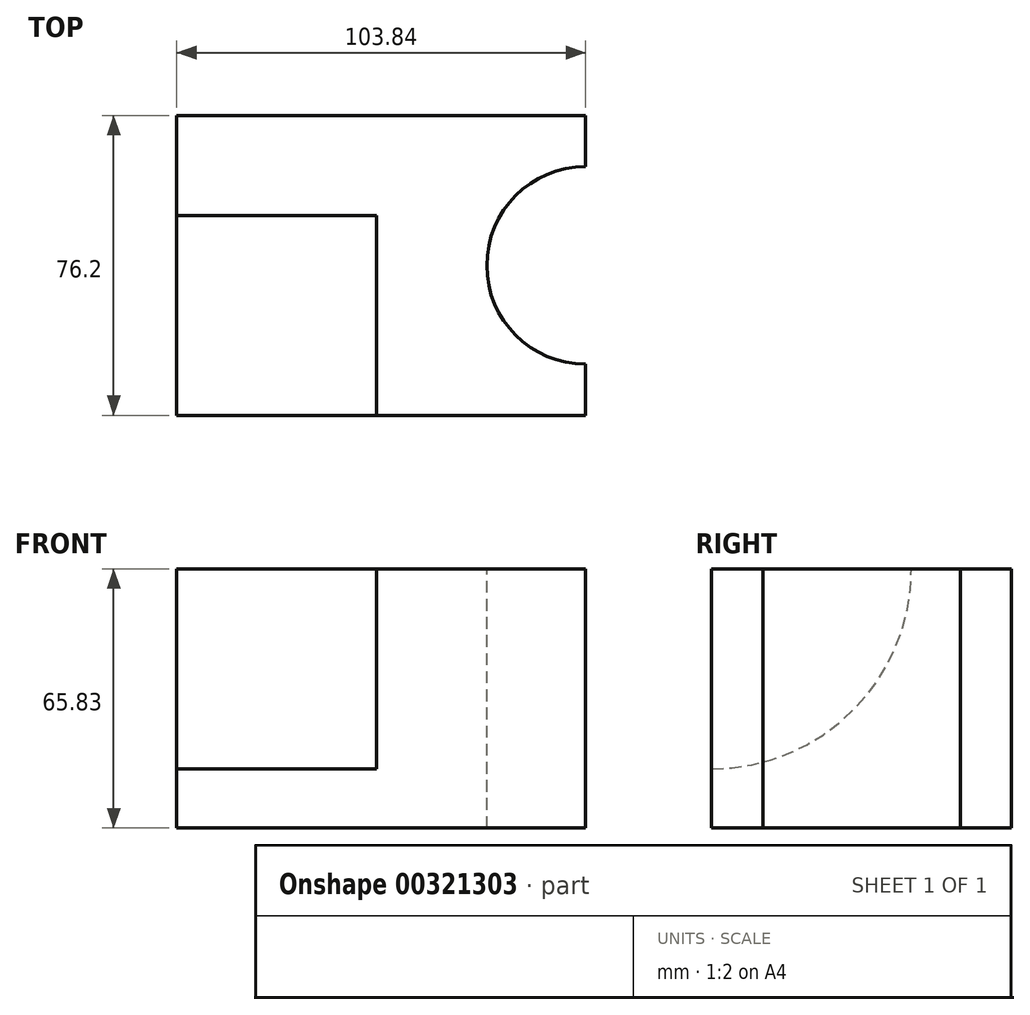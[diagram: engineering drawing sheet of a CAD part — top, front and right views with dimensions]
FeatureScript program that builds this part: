
annotation { "Feature Type Name" : "Feature", "Feature Type Description" : "" }
export const myFeature = defineFeature(function(context is Context, id is Id, definition is map)
    precondition{}
    {
        {
            var Q0;
            Q0=qCreatedBy(makeId("Front.planeOp"),FACE);
            var sketch = newSketch(context, id + "F0", { "sketchPlane" : qUnion([Q0])});
            skLineSegment(sketch, "E0", {"start": v(-57.31, -31.78) * mm, "end": v(46.53, -31.78) * mm});
            skLineSegment(sketch, "E1", {"start": v(46.53, -31.78) * mm, "end": v(46.53, 34.05) * mm});
            skLineSegment(sketch, "E2", {"start": v(46.53, 34.05) * mm, "end": v(-57.31, 34.05) * mm});
            skLineSegment(sketch, "E3", {"start": v(-57.31, 34.05) * mm, "end": v(-57.31, -31.78) * mm});
            skSolve(sketch);
        }
        {
            var Q0;
            Q0 = qSketchRegion(id + "F0", true);
            extrude(context, id + "F1", {"entities" : qUnion([Q0]), "depth" : 76.2 * mm});
        }
        {
            var Q0;
            Q0=makeQuery(id+"F1.opExtrude","SWEPT_FACE",FACE,{"disambiguationData":[OSD([sQuery(id+"F0.wireOp",EDGE,"E2")])]});
            var sketch = newSketch(context, id + "F2", { "sketchPlane" : qUnion([Q0])});
            skLineSegment(sketch, "E4", {"start": v(46.53, 0) * mm, "end": v(46.53, -12.7) * mm});
            skLineSegment(sketch, "E5", {"start": v(46.53, -76.2) * mm, "end": v(46.53, -63.5) * mm});
            skArc(sketch, "E6", {"start": v(46.53, -13.02) * mm, "mid": v(21.45, -38.1) * mm, "end": v(46.53, -63.18) * mm});
            skLineSegment(sketch, "E7", {"start": v(46.53, -12.7) * mm, "end": v(46.53, -63.5) * mm});
            skSolve(sketch);
        }
        {
            var Q0;
            Q0 = qSketchRegion(id + "F2", true);
            extrude(context, id + "F3", {"entities" : qUnion([Q0]), "operationType" : NewBodyOperationType.REMOVE, "oppositeDirection" : true, "depth" : 69.6 * mm});
        }
        {
            var Q0;
            Q0=makeQuery(id+"F1.opExtrude","SWEPT_FACE",FACE,{"disambiguationData":[OSD([sQuery(id+"F0.wireOp",EDGE,"E3")])]});
            var sketch = newSketch(context, id + "F4", { "sketchPlane" : qUnion([Q0])});
            skLineSegment(sketch, "E8", {"start": v(76.2, -31.78) * mm, "end": v(76.2, -19.08) * mm});
            skCircle(sketch, "E9", {"center": v(76.2, 34.05) * mm, "radius": 50.8 * mm});
            skLineSegment(sketch, "E10", {"start": v(25.4, 34.05) * mm, "end": v(76.2, 34.05) * mm});
            skSolve(sketch);
        }
        {
            var Q0;
            {var subQ0=sQuery(id+"F4.wireOp",EDGE,"E10");Q0=makeQuery(id+"F4.imprint","IMPRINT",FACE,{"disambiguationData":[TD([[makeQuery(id+"F4.imprint","IMPRINT",EDGE,{"derivedFrom":subQ0}),1.0]])]});}
            extrude(context, id + "F5", {"entities" : qUnion([Q0]), "operationType" : NewBodyOperationType.REMOVE, "oppositeDirection" : true, "depth" : 50.8 * mm});
        }
    });
